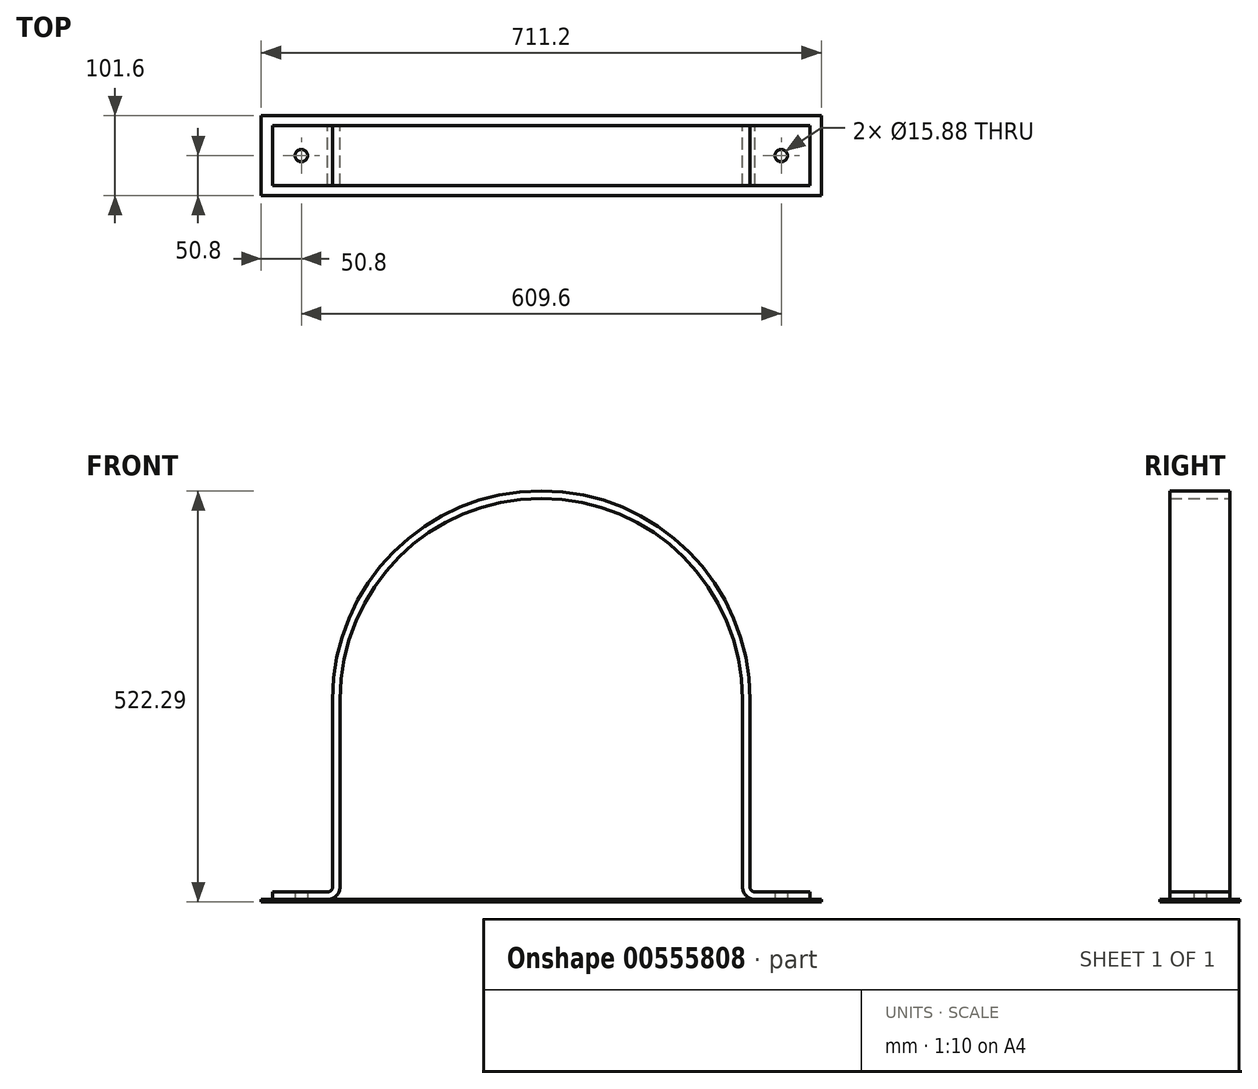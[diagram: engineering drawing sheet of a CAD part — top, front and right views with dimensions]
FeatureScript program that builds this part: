
annotation { "Feature Type Name" : "Feature", "Feature Type Description" : "" }
export const myFeature = defineFeature(function(context is Context, id is Id, definition is map)
    precondition{}
    {
        {
            var Q0;
            Q0=qCreatedBy(makeId("Front.planeOp"),FACE);
            var sketch = newSketch(context, id + "F0", { "sketchPlane" : qUnion([Q0])});
            skLineSegment(sketch, "E0.bottom", {"start": v(341.31, -254) * mm, "end": v(255.59, -254) * mm});
            skLineSegment(sketch, "E0.top", {"start": v(341.31, -244.47) * mm, "end": v(265.11, -244.47) * mm});
            skLineSegment(sketch, "E0.left", {"start": v(341.31, -254) * mm, "end": v(341.31, -244.47) * mm});
            skLineSegment(sketch, "E0.right", {"start": v(-341.31, -254) * mm, "end": v(-341.31, -244.48) * mm});
            skLineSegment(sketch, "E1", {"start": v(-255.59, 0) * mm, "end": v(-255.59, -254) * mm});
            skLineSegment(sketch, "E2", {"start": v(-265.11, 0) * mm, "end": v(-265.11, -244.48) * mm});
            skLineSegment(sketch, "E3", {"start": v(255.59, 0) * mm, "end": v(255.59, -254) * mm});
            skLineSegment(sketch, "E4", {"start": v(265.11, 0) * mm, "end": v(265.11, -244.48) * mm});
            skArc(sketch, "E5.trimOffspring", {"start": v(265.11, 0) * mm, "mid": v(0, 265.11) * mm, "end": v(-265.11, 0) * mm});
            skArc(sketch, "E6.trimOffspring", {"start": v(255.59, 0) * mm, "mid": v(0, 255.59) * mm, "end": v(-255.59, 0) * mm});
            skLineSegment(sketch, "E7.trimOffspring", {"start": v(-265.11, -244.48) * mm, "end": v(-341.31, -244.48) * mm});
            skLineSegment(sketch, "E8.trimOffspring", {"start": v(-255.59, -254) * mm, "end": v(-341.31, -254) * mm});
            skSolve(sketch);
        }
        {
            var Q0;
            Q0 = qSketchRegion(id + "F0", true);
            extrude(context, id + "F1", {"entities" : qUnion([Q0]), "endBound" : BoundingType.SYMMETRIC, "depth" : 76.2 * mm, "offsetDistance" : 25.4 * mm});
        }
        {
            var Q0;
            Q0=makeQuery(id+"F1.opExtrude","SWEPT_EDGE",EDGE,{"disambiguationData":[OSD([sQuery(id+"F0.wireOp",EDGE,"E2"),sQuery(id+"F0.wireOp",EDGE,"E7.trimOffspring")])]});
            var Q1;
            Q1=makeQuery(id+"F1.opExtrude","SWEPT_EDGE",EDGE,{"disambiguationData":[OSD([sQuery(id+"F0.wireOp",EDGE,"E0.top"),sQuery(id+"F0.wireOp",EDGE,"E4")])]});
            fillet(context, id + "F2", {"entities" : qUnion([Q0, Q1]), "radius" : 6.35 * mm, "tangentPropagation" : true, "allowEdgeOverflow" : false});
        }
        {
            var Q0;
            Q0=makeQuery(id+"F1.opExtrude","SWEPT_EDGE",EDGE,{"disambiguationData":[OSD([sQuery(id+"F0.wireOp",EDGE,"E1"),sQuery(id+"F0.wireOp",EDGE,"E8.trimOffspring")])]});
            var Q1;
            Q1=makeQuery(id+"F1.opExtrude","SWEPT_EDGE",EDGE,{"disambiguationData":[OSD([sQuery(id+"F0.wireOp",EDGE,"E0.bottom"),sQuery(id+"F0.wireOp",EDGE,"E3")])]});
            fillet(context, id + "F3", {"entities" : qUnion([Q0, Q1]), "radius" : 15.88 * mm, "tangentPropagation" : true, "allowEdgeOverflow" : false});
        }
        {
            var Q0;
            Q0=makeQuery(id+"F1.opExtrude","SWEPT_FACE",FACE,{"disambiguationData":[OSD([sQuery(id+"F0.wireOp",EDGE,"E8.trimOffspring")])]});
            var sketch = newSketch(context, id + "F4", { "sketchPlane" : qUnion([Q0])});
            skCircle(sketch, "E9", {"center": v(-304.8, 0) * mm, "radius": 7.94 * mm});
            skCircle(sketch, "E10.MirrorC", {"center": v(304.8, 0) * mm, "radius": 7.94 * mm});
            skSolve(sketch);
        }
        {
            var Q0;
            Q0 = qSketchRegion(id + "F4", true);
            extrude(context, id + "F5", {"entities" : qUnion([Q0]), "operationType" : NewBodyOperationType.REMOVE, "oppositeDirection" : true, "depth" : 25.4 * mm, "offsetDistance" : 25.4 * mm});
        }
        {
            var Q0;
            Q0=makeQuery(id+"F1.opExtrude","SWEPT_FACE",FACE,{"disambiguationData":[OSD([sQuery(id+"F0.wireOp",EDGE,"E0.bottom")])]});
            var sketch = newSketch(context, id + "F6", { "sketchPlane" : qUnion([Q0])});
            skLineSegment(sketch, "E11.bottom", {"start": v(355.6, -50.8) * mm, "end": v(-355.6, -50.8) * mm});
            skLineSegment(sketch, "E11.top", {"start": v(355.6, 50.8) * mm, "end": v(-355.6, 50.8) * mm});
            skLineSegment(sketch, "E11.left", {"start": v(355.6, -50.8) * mm, "end": v(355.6, 50.8) * mm});
            skLineSegment(sketch, "E11.right", {"start": v(-355.6, -50.8) * mm, "end": v(-355.6, 50.8) * mm});
            skPoint(sketch, "E11.middle", {"position": v(0, 0) * mm});
            skCircle(sketch, "E12", {"center": v(-304.8, 0) * mm, "radius": 7.94 * mm});
            skPoint(sketch, "E12.centerSnap0", {"position": v(-355.6, 0) * mm});
            skPoint(sketch, "E13.0", {"position": v(-341.31, -38.1) * mm});
            skLineSegment(sketch, "E14", {"start": v(-341.31, -38.1) * mm, "end": v(-341.31, 37.24) * mm, "construction": true});
            skCircle(sketch, "E15.MirrorC", {"center": v(304.8, 0) * mm, "radius": 7.94 * mm});
            skSolve(sketch);
        }
        {
            var Q0;
            Q0 = qSketchRegion(id + "F6", true);
            extrude(context, id + "F7", {"entities" : qUnion([Q0]), "operationType" : NewBodyOperationType.ADD, "depth" : 3.17 * mm, "offsetDistance" : 25.4 * mm});
        }
    });
